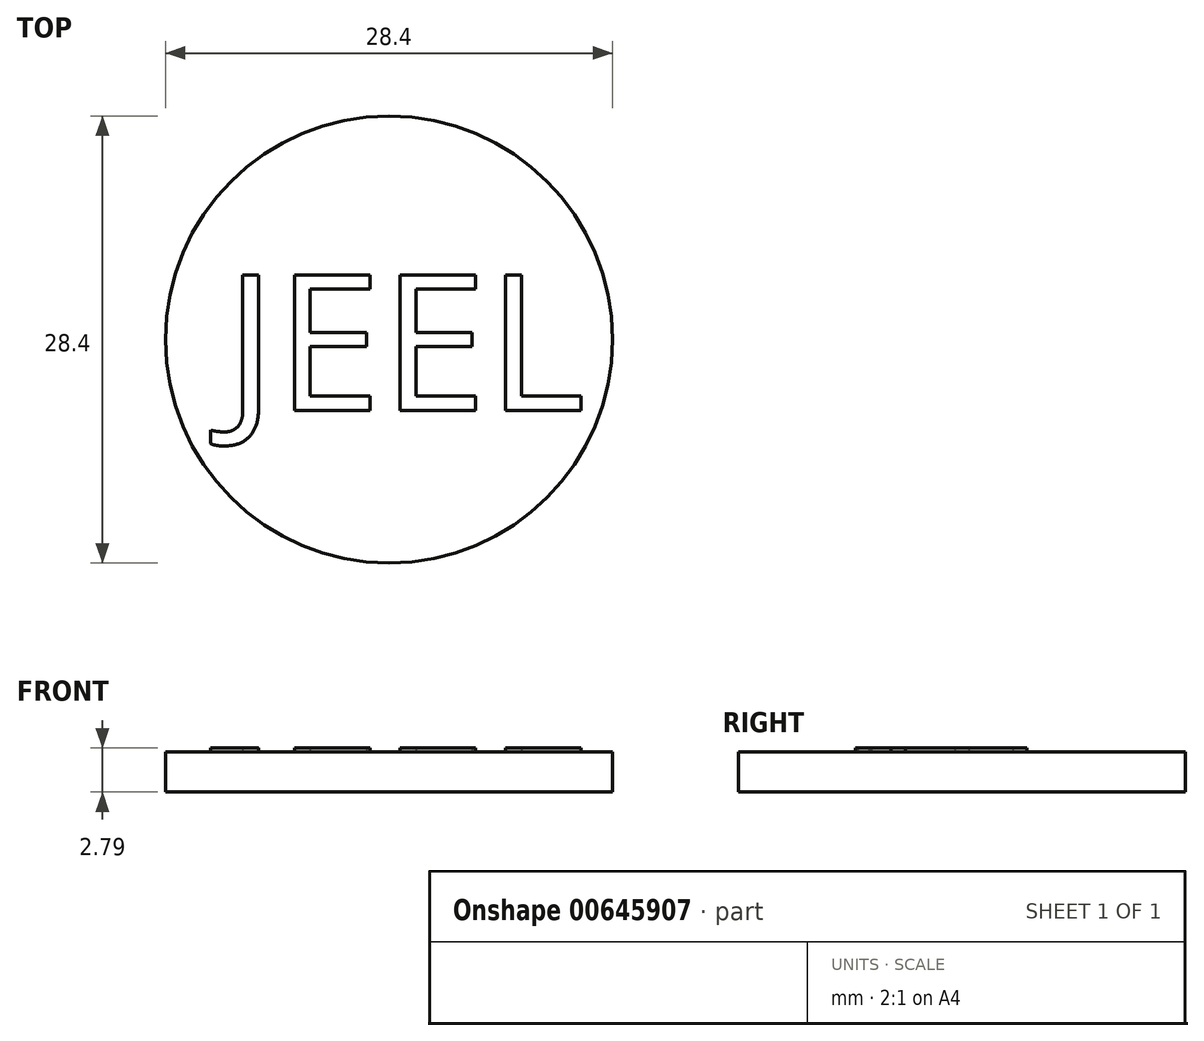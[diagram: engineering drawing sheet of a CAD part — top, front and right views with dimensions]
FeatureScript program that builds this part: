
annotation { "Feature Type Name" : "Feature", "Feature Type Description" : "" }
export const myFeature = defineFeature(function(context is Context, id is Id, definition is map)
    precondition{}
    {
        {
            var Q0;
            Q0=qCreatedBy(makeId("Top.planeOp"),FACE);
            var sketch = newSketch(context, id + "F0", { "sketchPlane" : qUnion([Q0])});
            skCircle(sketch, "E0", {"center": v(0, 0) * mm, "radius": 14.2 * mm});
            skSolve(sketch);
        }
        {
            var Q0;
            Q0 = qSketchRegion(id + "F0", true);
            extrude(context, id + "F1", {"entities" : qUnion([Q0]), "depth" : 2.54 * mm, "offsetDistance" : 25.4 * mm});
        }
        {
            var Q0;
            Q0=makeQuery(id+"F1.opExtrude","CAP_FACE",FACE,{"disambiguationData":[OSD([sQuery(id+"F0.wireOp",EDGE,"E0")])],"isStart":false});
            var sketch = newSketch(context, id + "F2", { "sketchPlane" : qUnion([Q0])});
            skText(sketch, "E1", { "text": "JEEL", "fontName": "OpenSans-Regular.ttf"});
            const initialGuessF2  = {"E1": [-0.0104, -0.0045, 1, 0, 0.00868]};
            skSetInitialGuess(sketch, initialGuessF2);
            skSolve(sketch);
        }
        {
            var Q0;
            Q0 = qSketchRegion(id + "F2", true);
            extrude(context, id + "F3", {"entities" : qUnion([Q0]), "operationType" : NewBodyOperationType.ADD, "depth" : 0.25 * mm, "offsetDistance" : 25.4 * mm});
        }
    });
